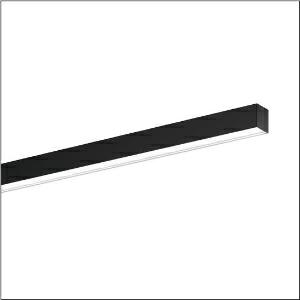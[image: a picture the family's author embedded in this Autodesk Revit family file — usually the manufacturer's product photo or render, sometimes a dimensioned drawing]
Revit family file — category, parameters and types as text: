
# Revit family: silica_r__21_51mx23tctab_c65d
name_source: partatom
category: Lighting Fixtures
units: mm (PartAtom-declared; Revit-internal decimal feet)

## family parameters
Cut with Voids When Loaded = No
Host = Face
Light Source = No
Part Type = Normal
Room Calculation Point = No
Round Connector Dimension = Use Diameter
Shared = No

## types (1)
- --- (1 x LED, 8070 lm, 81.1 W, 6500K)
    Apparent Load = 81 VA
    CIE Flux Codes = 78 96 99 100 100
    Color Rendering = 80
    Color Temperature = 6500K
    Default Elevation = 1800 mm
    Description = Silica® 21, office luminaire, primary optical cover: prismatic diffuser, of PMMA, CAT 2 (L<= 3000cd/m²), light emission: direct distribution, primary light characteristic: symmetric, installation type: surface-mounted, LED, rated luminous flux: 8.070lm, luminous efficacy: 95lm/W, light colour: 8tw, colour temperature: 2700..6500K, control gear: ECG DALI, with terminal, 3+2-pole, max. 2.5mm², mains connection: 220..240V, AC, 50/60Hz, rated input power: 85.1W, luminaire housing, of aluminium, jet black (RAL 9005), length: 3.004mm, width: 53mm, height: 53mm, protection rating (complete): IP20, insulation class (complete): insulation class I (protective earthing), certification: CE, permissible operating ambient temperature: 0..+35°C, standard: EN 50419, packaging unit: 1 piece
    Height = 0 mm  [stored 0 ft]
    Lamp = 1 x LED
    Lamp Light Flux = 8070 lm
    Lamp Power = 81.1 W
    Lamp count = 1
    Length = 3004 mm
    Luminous efficacy = 100 lm/W
    Manufacturer = Siteco
    ModVariant = No
    Model = 51MX23TCTAB
    Mounting Place = Ceiling
    Mounting Type = Recessed
    Number of Poles = 1
    OnlyDefault = Yes
    Power Factor = 1
    Product Name = Silica® 21
    Product group = office luminaire | ceiling recessed
    ProductGroupID = 401
    Protection Class = Protection class I
    Protection Degree = IP 20
    RLX_Detail_Level = 1
    RLX_Emergency_Light_Flux = 0 lm
    RLX_Emergency_Type = 0
    RLX_Emergency_Type_DB = No
    RlxData = <blob elided: 20405 chars, md5=c323c446>
    Socket = socket
    Standby Power = 0 W
    System Light Flux = 8070 lm
    System Power = 81 W
    Type Comments = individual setting
    Type Image = l_1297760.jpg
    URL = http://relux.com
    VarID = @adj_071131
    Voltage = 0 V
    Weight = 0.00 kg
    Width = 53 mm

note: [stored X ft] marks values corroborated as IEEE doubles in the binary element streams (Revit-internal decimal feet)

## geometry (parser evidence)
native form markers: Blend x4, Sweep x10
no freeform markers — native parametric forms only
